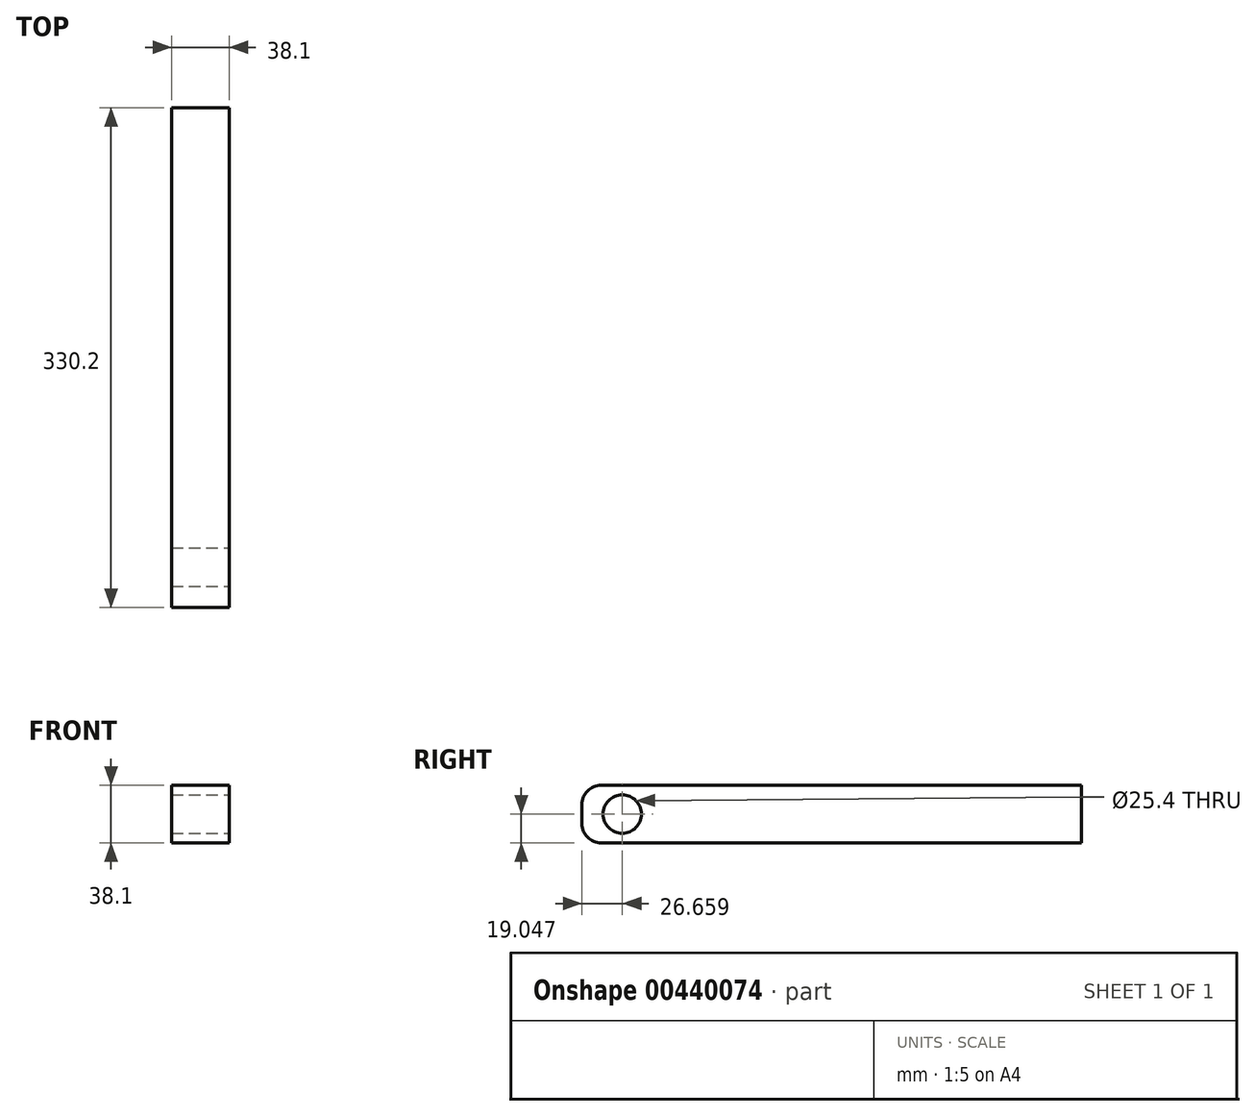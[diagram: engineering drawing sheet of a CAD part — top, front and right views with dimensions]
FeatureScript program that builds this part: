
annotation { "Feature Type Name" : "Feature", "Feature Type Description" : "" }
export const myFeature = defineFeature(function(context is Context, id is Id, definition is map)
    precondition{}
    {
        {
            var Q0;
            Q0=qCreatedBy(makeId("Front.planeOp"),FACE);
            var sketch = newSketch(context, id + "F0", { "sketchPlane" : qUnion([Q0])});
            skLineSegment(sketch, "E0.bottom", {"start": v(-22.73, -15.74) * mm, "end": v(15.37, -15.74) * mm});
            skLineSegment(sketch, "E0.top", {"start": v(-22.73, 22.36) * mm, "end": v(15.37, 22.36) * mm});
            skLineSegment(sketch, "E0.left", {"start": v(-22.73, -15.74) * mm, "end": v(-22.73, 22.36) * mm});
            skLineSegment(sketch, "E0.right", {"start": v(15.37, -15.74) * mm, "end": v(15.37, 22.36) * mm});
            skSolve(sketch);
        }
        {
            var Q0;
            Q0 = qSketchRegion(id + "F0", true);
            extrude(context, id + "F1", {"entities" : qUnion([Q0]), "depth" : 330.2 * mm});
        }
        {
            var Q0;
            Q0=makeQuery(id+"F1.opExtrude","SWEPT_FACE",FACE,{"disambiguationData":[OSD([sQuery(id+"F0.wireOp",EDGE,"E0.right")])]});
            var sketch = newSketch(context, id + "F2", { "sketchPlane" : qUnion([Q0])});
            skCircle(sketch, "E1", {"center": v(-303.54, 3.3) * mm, "radius": 12.7 * mm});
            skPoint(sketch, "E1.centerSnap0", {"position": v(-330.2, 3.3) * mm});
            skSolve(sketch);
        }
        {
            var Q0;
            Q0 = qSketchRegion(id + "F2", true);
            extrude(context, id + "F3", {"entities" : qUnion([Q0]), "operationType" : NewBodyOperationType.REMOVE, "endBound" : BoundingType.THROUGH_ALL, "oppositeDirection" : true, "depth" : 25.4 * mm});
        }
        {
            var Q0;
            Q0=makeQuery(id+"F1.opExtrude","CAP_EDGE",EDGE,{"disambiguationData":[OSD([sQuery(id+"F0.wireOp",EDGE,"E0.top")])],"isStart":false});
            var Q1;
            Q1=makeQuery(id+"F1.opExtrude","CAP_EDGE",EDGE,{"disambiguationData":[OSD([sQuery(id+"F0.wireOp",EDGE,"E0.bottom")])],"isStart":false});
            fillet(context, id + "F4", {"entities" : qUnion([Q0, Q1]), "radius" : 12.7 * mm, "tangentPropagation" : true, "allowEdgeOverflow" : false});
        }
    });
